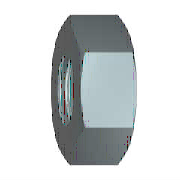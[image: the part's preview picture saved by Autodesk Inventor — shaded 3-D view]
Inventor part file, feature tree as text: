
AUTODESK INVENTOR PART (.ipt)
format: ipt  version: 2024.2 (Build 282272000, 272)  size: 163,328 bytes
history: native  units: mm (DEFAULTED — no unit token found)
features: chamfer x1, hole x1, other x1, plane x1
ambient origin geometry x7: Origin, YZ Plane, XZ Plane, X Axis, Y Axis, Z Axis, Center Point
bodies: Solid1 (feature_tree), Body (feature_tree)
feature tree (4):
  chamfer  "Chamfer1"  Distance=18.475209mm
  hole  "Thread"  [1 undecoded]
  other  "Work Axis1"
  plane  "Work Plane1"
note: 1 required parameter value undecoded (feature->parameter linkage not recoverable at this tier; creation-order binding heuristic only, values carry confidence <= 0.55)
